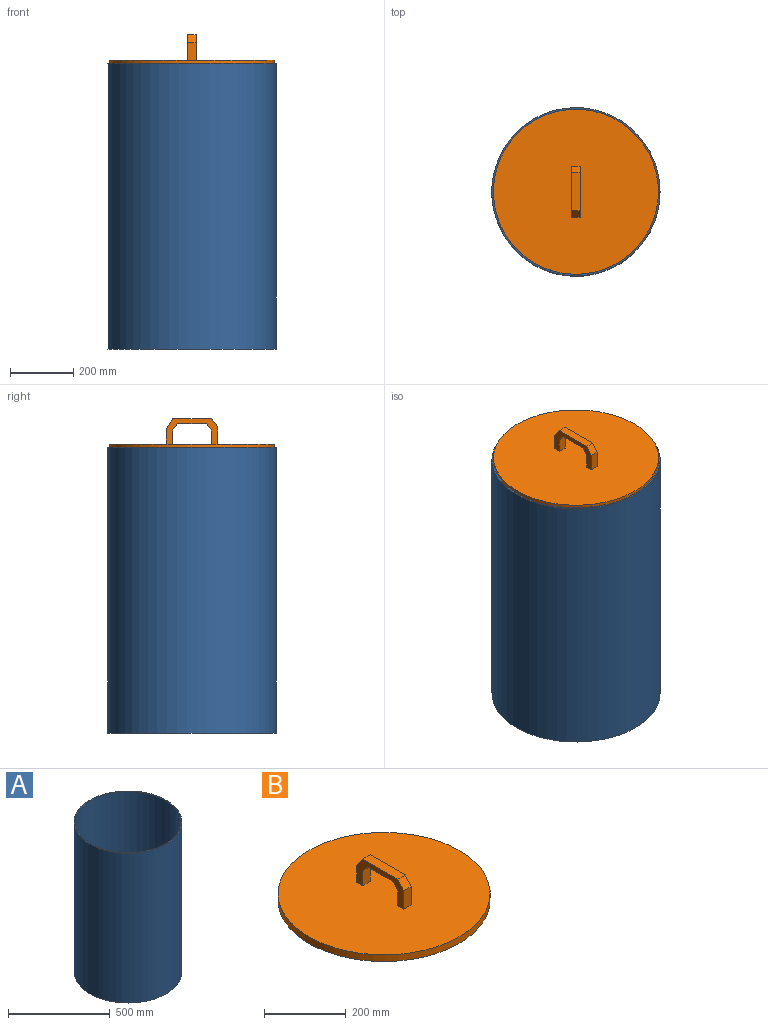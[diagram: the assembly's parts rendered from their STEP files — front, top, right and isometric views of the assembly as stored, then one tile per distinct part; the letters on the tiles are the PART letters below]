
ASSEMBLY  parts=2 mates=1
PART A: 5 faces, bbox 530x530x900 mm
  f0: cylinder r=265mm len=900mm, axis (0,0,-1), area 1498539.7mm2, adj f1,f2
  f1: plane 530x530mm, normal (0,0,1), area 8246.7mm2, adj f0,f3
  f2: plane 530x530mm, normal (0,0,-1), area 220618.3mm2, adj f0
  f3: cylinder r=260mm len=890mm, axis (0,0,1), area 1453929.1mm2, adj f1,f4
  f4: plane 520x520mm, normal (0,0,1), area 212371.7mm2, adj f3
PART B: 15 faces, bbox 520x520x100 mm
  f0: plane 121.51x26.13mm, normal (0,0,1), area 3174.9mm2, adj f1,f2,f13,f14
  f1: plane 161.51x80mm, normal (1,0,0), area 4785.5mm2, adj f0,f3,f6,f7,f8,f9,f10,f11
  f2: plane 161.51x80mm, normal (-1,0,0), area 4785.5mm2, adj f0,f3,f6,f7,f8,f9,f10,f11
  f3: plane 520x520mm, normal (0,0,1), area 211326.5mm2, adj f1,f2,f4,f6,f7,f10,f11
  f4: cylinder r=260mm len=520mm, axis (0,0,-1), area 32672.6mm2, adj f3,f5
  f5: plane 520x520mm, normal (0,0,-1), area 212371.7mm2, adj f4
  f6: plane 54.61x26.13mm, normal (0,-1,0), area 1426.9mm2, adj f1,f2,f3,f13
  f7: plane 50.16x26.13mm, normal (0,1,0), area 1310.7mm2, adj f1,f2,f3,f14
  f8: plane 90x26.13mm, normal (0,0,-1), area 2351.6mm2, adj f1,f2,f9,f12
  f9: plane 26.13x20mm, normal (0,0.79,-0.62), area 665.2mm2, adj f1,f2,f8,f10
  f10: plane 45x26.13mm, normal (0,1,0), area 1175.8mm2, adj f1,f2,f3,f9
  f11: plane 45x26.13mm, normal (0,-1,0), area 1175.8mm2, adj f1,f2,f3,f12
  f12: plane 26.13x20mm, normal (0,-0.79,-0.62), area 665.2mm2, adj f1,f2,f8,f11
  f13: plane 26.13x25.39mm, normal (0,-0.79,0.62), area 844.5mm2, adj f0,f1,f2,f6
  f14: plane 29.84x26.13mm, normal (0,0.83,0.56), area 938.6mm2, adj f0,f1,f2,f7
PLACE A at identity
PLACE B t=(0,0,890)mm
MATE fastened B.f4 <-> A.f3  axis (0,0,-1) through (0,0,900)mm
